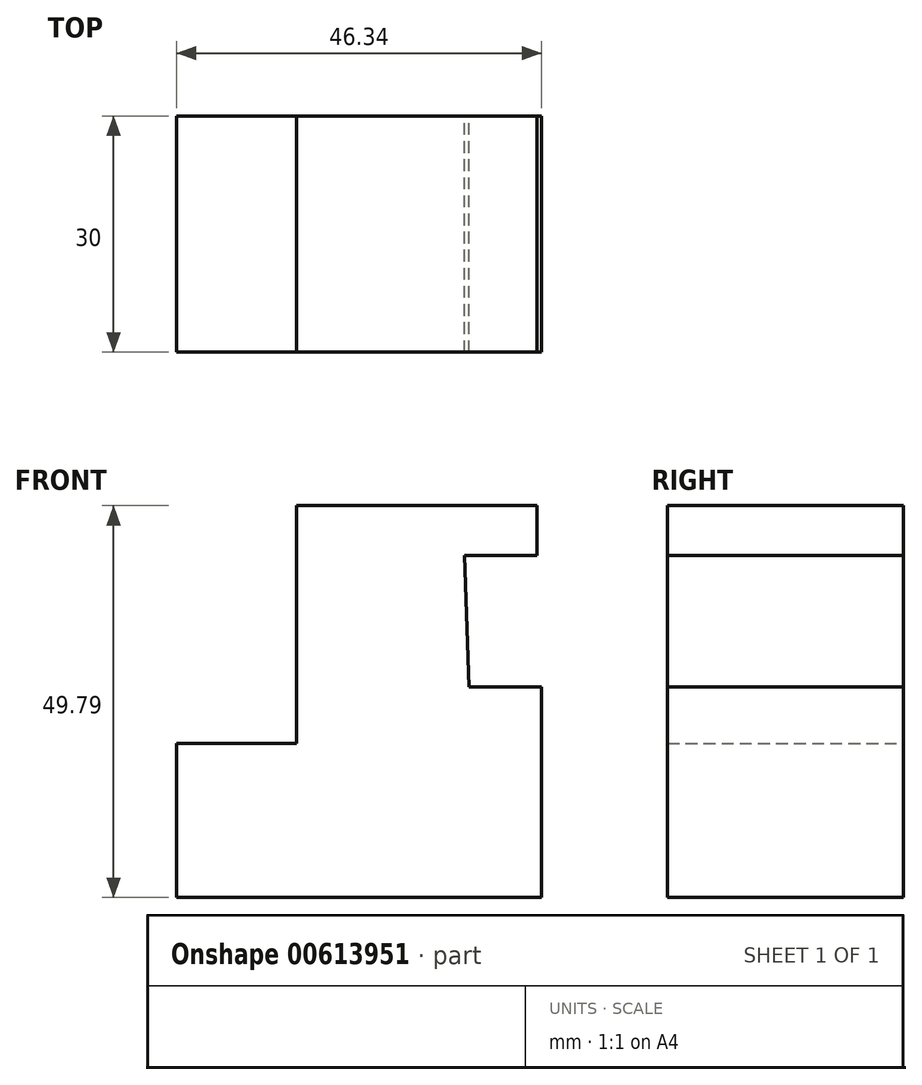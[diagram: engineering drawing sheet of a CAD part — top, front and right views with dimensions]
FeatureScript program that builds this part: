
annotation { "Feature Type Name" : "Feature", "Feature Type Description" : "" }
export const myFeature = defineFeature(function(context is Context, id is Id, definition is map)
    precondition{}
    {
        {
            var Q0;
            Q0=qCreatedBy(makeId("Front.planeOp"),FACE);
            var sketch = newSketch(context, id + "F0", { "sketchPlane" : qUnion([Q0])});
            skLineSegment(sketch, "E0", {"start": v(-35.83, 34.4) * mm, "end": v(-35.83, 4.17) * mm});
            skLineSegment(sketch, "E1", {"start": v(-35.83, 4.17) * mm, "end": v(-51.09, 4.17) * mm});
            skLineSegment(sketch, "E2", {"start": v(-51.09, 4.17) * mm, "end": v(-51.09, -15.4) * mm});
            skLineSegment(sketch, "E3", {"start": v(-51.09, -15.4) * mm, "end": v(-4.75, -15.4) * mm});
            skLineSegment(sketch, "E4", {"start": v(-4.75, -15.4) * mm, "end": v(-4.75, 11.37) * mm});
            skLineSegment(sketch, "E5", {"start": v(-4.75, 11.37) * mm, "end": v(-13.96, 11.37) * mm});
            skPoint(sketch, "E6.start.orphan", {"position": v(-13.96, 34.4) * mm});
            skLineSegment(sketch, "E7", {"start": v(-35.83, 34.4) * mm, "end": v(-5.32, 34.4) * mm});
            skLineSegment(sketch, "E8", {"start": v(-5.32, 34.4) * mm, "end": v(-5.32, 28.06) * mm});
            skLineSegment(sketch, "E9", {"start": v(-5.32, 28.06) * mm, "end": v(-14.53, 28.06) * mm});
            skLineSegment(sketch, "E10", {"start": v(-14.53, 28.06) * mm, "end": v(-13.96, 11.37) * mm});
            skSolve(sketch);
        }
        {
            var Q0;
            Q0 = qSketchRegion(id + "F0", true);
            extrude(context, id + "F1", {"entities" : qUnion([Q0]), "depth" : 30 * mm, "offsetDistance" : 25 * mm});
        }
    });
